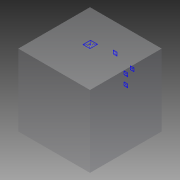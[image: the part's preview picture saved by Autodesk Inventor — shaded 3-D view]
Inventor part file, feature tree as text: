
AUTODESK INVENTOR PART (.ipt)
format: ipt  version: 2014 (Build 180170000, 170)  size: 446,464 bytes
history: native  units: mm
features: other x53, sketch x6, extrude x1
ambient origin geometry x8: Origin, YZ Plane, XZ Plane, XY Plane, X Axis, Y Axis, Z Axis, Center Point
bodies: 实体1 (feature_tree)
feature tree (60):
  extrude  "拉伸1"  TaperAngle=0.0deg  [1 undecoded]
  other  "UCS1"
  other  "UCS2"
  other  "UCS3"
  other  "UCS4"
  other  "UCS5"
  other  "UCS6"
  other  "Footprint1"
  other  "Footprint2"
  other  "Footprint3"
  other  "Footprint4"
  other  "Footprint5"
  sketch  "草图1"  dims[d0=1000.0mm d1=0.0mm]
  other  "UCS1: YZ 平面"
  other  "UCS1: XZ 平面"
  other  "UCS1: XY 平面"
  other  "UCS1: X 轴"
  other  "UCS1: Y 轴"
  other  "UCS1: Z 轴"
  other  "UCS1: 原点"
  other  "UCS2: YZ 平面"
  other  "UCS2: XZ 平面"
  other  "UCS2: XY 平面"
  other  "UCS2: X 轴"
  other  "UCS2: Y 轴"
  other  "UCS2: Z 轴"
  other  "UCS2: 原点"
  other  "UCS3: YZ 平面"
  other  "UCS3: XZ 平面"
  other  "UCS3: XY 平面"
  other  "UCS3: X 轴"
  other  "UCS3: Y 轴"
  other  "UCS3: Z 轴"
  other  "UCS3: 原点"
  other  "UCS4: YZ 平面"
  other  "UCS4: XZ 平面"
  other  "UCS4: XY 平面"
  other  "UCS4: X 轴"
  other  "UCS4: Y 轴"
  other  "UCS4: Z 轴"
  other  "UCS4: 原点"
  other  "UCS5: YZ 平面"
  other  "UCS5: XZ 平面"
  other  "UCS5: XY 平面"
  other  "UCS5: X 轴"
  other  "UCS5: Y 轴"
  other  "UCS5: Z 轴"
  other  "UCS5: 原点"
  other  "UCS6: YZ 平面"
  other  "UCS6: XZ 平面"
  other  "UCS6: XY 平面"
  other  "UCS6: X 轴"
  other  "UCS6: Y 轴"
  other  "UCS6: Z 轴"
  other  "UCS6: 原点"
  sketch  "草图4"  dims[d8=0.0mm d9=0.0mm d10=0.0mm d11=0.0mm d12=0.0mm d13=0.0mm]
  sketch  "草图6"  dims[d14=0.0mm d15=0.0mm d16=0.0mm d17=0.0mm d18=0.0mm d19=0.0mm]
  sketch  "草图8"  dims[d20=0.0mm d21=0.0mm d22=0.0mm d23=0.0mm d24=0.0mm d25=0.0mm]
  sketch  "草图10"  dims[d26=0.0mm d27=0.0mm d28=0.0mm d29=0.0mm d30=0.0mm d31=0.0mm d32=0.0mm d33=0.0mm d34=0.0mm d35=0.0mm d36=0.0mm d37=0.0mm d38=0.0mm d52=0.0mm d53=0.0mm d67=0.0mm d81=0.0mm d95=0.0mm d96=0.0mm d97=0.0mm d98=0.0mm d112=0.0mm]
  sketch  "草图2"  dims[d2=0.0mm d3=0.0mm d4=0.0mm d5=0.0mm d6=0.0mm d7=0.0mm]
note: 1 required parameter value undecoded (feature->parameter linkage not recoverable at this tier; creation-order binding heuristic only, values carry confidence <= 0.55)
